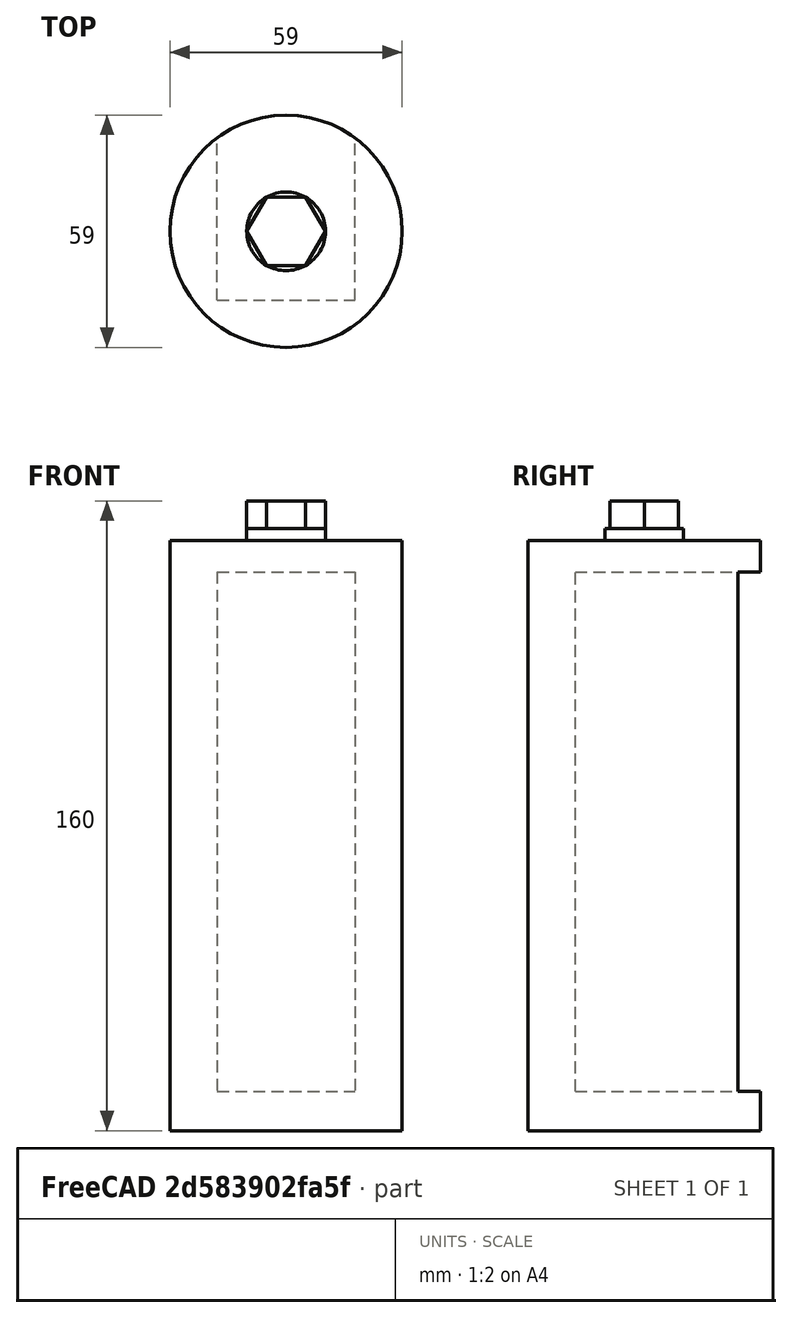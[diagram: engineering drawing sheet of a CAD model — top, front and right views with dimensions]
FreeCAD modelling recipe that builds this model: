
FCSTD DOCUMENT  (FreeCAD 0.20R29603 (Git))
Label: Eisdosierer_walze2
License: All rights reserved
LicenseURL: http://en.wikipedia.org/wiki/All_rights_reserved
objects: TechDraw::DrawViewDimension×11, TechDraw::DrawViewPart×3, PartDesign::AdditiveCylinder×2, PartDesign::SubtractiveBox×1, PartDesign::AdditivePrism×1, PartDesign::Body×1, TechDraw::DrawSVGTemplate×1, TechDraw::DrawViewSection×1, TechDraw::DrawPage×1
note: 9 computed .brp shape members not serialized (recipe doc carries the construction recipe); baked Part::Feature solids carry a one-line shape summary decoded from their .brp

FEATURE [PartDesign::AdditiveCylinder] Cylinder
  Angle = 360
  AttacherType = Attacher::AttachEngine3D
  FirstAngle = 0
  Height = 150
  MapMode = 5
  Radius = 29.5
  SecondAngle = 0
FEATURE [PartDesign::SubtractiveBox] Box
  AttacherType = Attacher::AttachEngine3D
  AttachmentOffset = pos=(-17.5,-17.5,10) rot=(0,0,1;0rad)
  BaseFeature = -> Cylinder
  Height = 132
  Length = 35
  MapMode = 2
  Placement = pos=(-17.5,-17.5,10) rot=(0,0,1;0rad)
  Support = -> [Cylinder]
  Width = 50
FEATURE [PartDesign::AdditiveCylinder] Cylinder001
  Angle = 360
  AttacherType = Attacher::AttachEngine3D
  BaseFeature = -> Box
  FirstAngle = 0
  Height = 3
  MapMode = 45
  Placement = pos=(-7.1e-15,0,150) rot=(0,0,1;0rad)
  Radius = 10
  SecondAngle = 0
  Support = -> [Box]
FEATURE [PartDesign::AdditivePrism] Prism
  AttacherType = Attacher::AttachEngine3D
  BaseFeature = -> Cylinder001
  Circumradius = 10
  FirstAngle = 0
  Height = 7
  MapMode = 5
  Placement = pos=(-7.1e-15,0,153) rot=(0,0,1;0rad)
  Polygon = 6
  SecondAngle = 0
  Support = -> [Cylinder001]
FEATURE [PartDesign::Body] Body
  Group = -> [Cylinder,Box,Cylinder001,Prism]
  Origin = -> Origin
  Tip = -> Prism
FEATURE [TechDraw::DrawSVGTemplate] Template
  EditableTexts = Designed_by_Name=B. Schulze; Drawing_number=1; FC-Date=03.08.2023; FC-SC=1:1; FC-SH=3; FC-Title=Eisdosierer; Subtitle=Walze
  Height = 210
  Orientation = 1
  Width = 297
FEATURE [TechDraw::DrawViewPart] View  label="Rechts"
  Caption = Rechts
  CoarseView = false
  Direction = (0,0,1)
  Focus = 100
  HardHidden = false
  IsoCount = 0
  IsoHidden = false
  IsoVisible = false
  LockPosition = false
  Perspective = false
  Rotation = 0
  ScaleType = 0
  SeamHidden = false
  SeamVisible = true
  SmoothHidden = false
  SmoothVisible = true
  Source = -> [Body]
  X = 44.125
  XDirection = (1,0,0)
  Y = 54.5714
FEATURE [TechDraw::DrawViewDimension] Dimension
  AngleOverride = false
  Arbitrary = false
  ArbitraryTolerances = false
  EqualTolerance = true
  ExtensionAngle = 0
  FormatSpec = ⌀%.2w
  FormatSpecOverTolerance = %+.2w
  FormatSpecUnderTolerance = %+.2w
  Inverted = false
  LineAngle = 0
  LockPosition = false
  MeasureType = 1
  OverTolerance = 0
  References2D = -> [View]
  Rotation = 0
  ScaleType = 0
  TheoreticalExact = false
  Type = 5
  UnderTolerance = 0
  X = 20.6256
  Y = 5.77337
FEATURE [TechDraw::DrawViewDimension] Dimension001
  AngleOverride = false
  Arbitrary = false
  ArbitraryTolerances = false
  EqualTolerance = true
  ExtensionAngle = 0
  FormatSpec = ⌀%.2w
  FormatSpecOverTolerance = %+.2w
  FormatSpecUnderTolerance = %+.2w
  Inverted = false
  LineAngle = 0
  LockPosition = false
  MeasureType = 1
  OverTolerance = 0
  References2D = -> [View]
  Rotation = 0
  ScaleType = 0
  TheoreticalExact = false
  Type = 5
  UnderTolerance = 0
  X = -21.1703
  Y = -5.20288
FEATURE [TechDraw::DrawViewDimension] Dimension002
  AngleOverride = false
  Arbitrary = false
  ArbitraryTolerances = false
  EqualTolerance = true
  ExtensionAngle = 0
  FormatSpec = %.2w
  FormatSpecOverTolerance = %+.2w
  FormatSpecUnderTolerance = %+.2w
  Inverted = false
  LineAngle = 0
  LockPosition = false
  MeasureType = 1
  OverTolerance = 0
  References2D = -> [View]
  Rotation = 0
  ScaleType = 0
  TheoreticalExact = false
  Type = 1
  UnderTolerance = 0
  X = 0.448524
  Y = -11.393
FEATURE [TechDraw::DrawViewPart] View001  label="Oben"
  Caption = Oben
  CoarseView = false
  Direction = (0,1,0)
  Focus = 100
  HardHidden = false
  IsoCount = 0
  IsoHidden = false
  IsoVisible = false
  LockPosition = false
  Perspective = false
  Rotation = 0
  ScaleType = 0
  SeamHidden = false
  SeamVisible = true
  SmoothHidden = false
  SmoothVisible = true
  Source = -> [Body]
  X = 103.455
  XDirection = (0,0,-1)
  Y = 153.124
FEATURE [TechDraw::DrawViewDimension] Dimension003
  AngleOverride = false
  Arbitrary = false
  ArbitraryTolerances = false
  EqualTolerance = true
  ExtensionAngle = 0
  FormatSpec = %.2w
  FormatSpecOverTolerance = %+.2w
  FormatSpecUnderTolerance = %+.2w
  Inverted = false
  LineAngle = 0
  LockPosition = false
  MeasureType = 1
  OverTolerance = 0
  References2D = -> [View001]
  Rotation = 0
  ScaleType = 0
  TheoreticalExact = false
  Type = 1
  UnderTolerance = 0
  X = 6.99219
  Y = 42.1883
FEATURE [TechDraw::DrawViewDimension] Dimension004
  AngleOverride = false
  Arbitrary = false
  ArbitraryTolerances = false
  EqualTolerance = true
  ExtensionAngle = 0
  FormatSpec = %.2w
  FormatSpecOverTolerance = %+.2w
  FormatSpecUnderTolerance = %+.2w
  Inverted = false
  LineAngle = 0
  LockPosition = false
  MeasureType = 1
  OverTolerance = 0
  References2D = -> [View001]
  Rotation = 0
  ScaleType = 0
  TheoreticalExact = false
  Type = 1
  UnderTolerance = 0
  X = 5.17713
  Y = 10.6268
FEATURE [TechDraw::DrawViewDimension] Dimension006
  AngleOverride = false
  Arbitrary = false
  ArbitraryTolerances = false
  EqualTolerance = true
  ExtensionAngle = 0
  FormatSpec = %.2w
  FormatSpecOverTolerance = %+.2w
  FormatSpecUnderTolerance = %+.2w
  Inverted = false
  LineAngle = 0
  LockPosition = false
  MeasureType = 1
  OverTolerance = 0
  References2D = -> [View001]
  Rotation = 0
  ScaleType = 0
  TheoreticalExact = false
  Type = 1
  UnderTolerance = 0
  X = -71.695
  Y = -34.561
FEATURE [TechDraw::DrawViewDimension] Dimension007
  AngleOverride = false
  Arbitrary = false
  ArbitraryTolerances = false
  EqualTolerance = true
  ExtensionAngle = 0
  FormatSpec = %.2w
  FormatSpecOverTolerance = %+.2w
  FormatSpecUnderTolerance = %+.2w
  Inverted = false
  LineAngle = 0
  LockPosition = false
  MeasureType = 1
  OverTolerance = 0
  References2D = -> [View001]
  Rotation = 0
  ScaleType = 0
  TheoreticalExact = false
  Type = 1
  UnderTolerance = 0
  X = -77.8557
  Y = 27.24
FEATURE [TechDraw::DrawViewSection] SectionView  label="Schnitt"
  BaseView = -> View001
  Caption = Schnitt
  CoarseView = false
  CutSurfaceDisplay = 2
  Direction = (0,0,-1)
  FileGeomPattern = <path> 0.20/data/Mod/TechDraw/PAT/FCPAT.pat
  FileHatchPattern = <path> 0.20/data/Mod/TechDraw/Patterns/simple.svg
  Focus = 100
  FuseBeforeCut = false
  HardHidden = false
  HatchScale = 1
  IsoCount = 0
  IsoHidden = false
  IsoVisible = false
  LockPosition = false
  NameGeomPattern = Diamond
  Perspective = false
  Rotation = 0
  ScaleType = 0
  SeamHidden = false
  SeamVisible = true
  SectionDirection = 1
  SectionNormal = (0,0,-1)
  SectionOrigin = (0,0,79.95)
  SectionSymbol = Schnitt
  SmoothHidden = false
  SmoothVisible = true
  Source = -> [Body]
  X = 238.159
  XDirection = (0,-1,0)
  Y = 151.247
FEATURE [TechDraw::DrawViewDimension] Dimension008
  AngleOverride = false
  Arbitrary = false
  ArbitraryTolerances = false
  EqualTolerance = true
  ExtensionAngle = 0
  FormatSpec = %.2w
  FormatSpecOverTolerance = %+.2w
  FormatSpecUnderTolerance = %+.2w
  Inverted = false
  LineAngle = 0
  LockPosition = false
  MeasureType = 1
  OverTolerance = 0
  References2D = -> [SectionView]
  Rotation = 0
  ScaleType = 0
  TheoreticalExact = false
  Type = 2
  UnderTolerance = 0
  X = 5.33065
  Y = 5.04707
FEATURE [TechDraw::DrawViewDimension] Dimension009
  AngleOverride = false
  Arbitrary = false
  ArbitraryTolerances = false
  EqualTolerance = true
  ExtensionAngle = 0
  FormatSpec = %.2w
  FormatSpecOverTolerance = %+.2w
  FormatSpecUnderTolerance = %+.2w
  Inverted = false
  LineAngle = 0
  LockPosition = false
  MeasureType = 1
  OverTolerance = 0
  References2D = -> [SectionView]
  Rotation = 0
  ScaleType = 0
  TheoreticalExact = false
  Type = 1
  UnderTolerance = 0
  X = -2.27532
  Y = 41.2256
FEATURE [TechDraw::DrawViewDimension] Dimension010
  AngleOverride = false
  Arbitrary = false
  ArbitraryTolerances = false
  EqualTolerance = true
  ExtensionAngle = 0
  FormatSpec = %.2w
  FormatSpecOverTolerance = %+.2w
  FormatSpecUnderTolerance = %+.2w
  Inverted = false
  LineAngle = 0
  LockPosition = false
  MeasureType = 1
  OverTolerance = 0
  References2D = -> [SectionView]
  Rotation = 0
  ScaleType = 0
  TheoreticalExact = false
  Type = 1
  UnderTolerance = 0
  X = 26.8944
  Y = -26.0091
FEATURE [TechDraw::DrawViewPart] View002  label="Links"
  Caption = Links
  CoarseView = false
  Direction = (0,0,-1)
  Focus = 100
  HardHidden = false
  IsoCount = 0
  IsoHidden = false
  IsoVisible = false
  LockPosition = false
  Perspective = false
  Rotation = 0
  ScaleType = 0
  SeamHidden = false
  SeamVisible = true
  SmoothHidden = false
  SmoothVisible = true
  Source = -> [Cylinder]
  X = 113.679
  XDirection = (0,-1,0)
  Y = 55.8929
FEATURE [TechDraw::DrawViewDimension] Dimension011
  AngleOverride = false
  Arbitrary = false
  ArbitraryTolerances = false
  EqualTolerance = true
  ExtensionAngle = 0
  FormatSpec = ⌀%.2w
  FormatSpecOverTolerance = %+.2w
  FormatSpecUnderTolerance = %+.2w
  Inverted = false
  LineAngle = 0
  LockPosition = false
  MeasureType = 1
  OverTolerance = 0
  References2D = -> [View002]
  Rotation = 0
  ScaleType = 0
  TheoreticalExact = false
  Type = 5
  UnderTolerance = 0
  X = 11.1607
  Y = 5.35714
FEATURE [TechDraw::DrawPage] Page
  KeepUpdated = true
  NextBalloonIndex = 1
  ProjectionType = 0
  Template = -> Template
  Views = -> [View,Dimension,Dimension001,Dimension002,View001,Dimension003,Dimension004,Dimension006,Dimension007,SectionView,Dimension008,Dimension009,Dimension010,View002,Dimension011]
note: 2 file-system paths scrubbed to <path> (originals preserved in the JSON sidecar)
